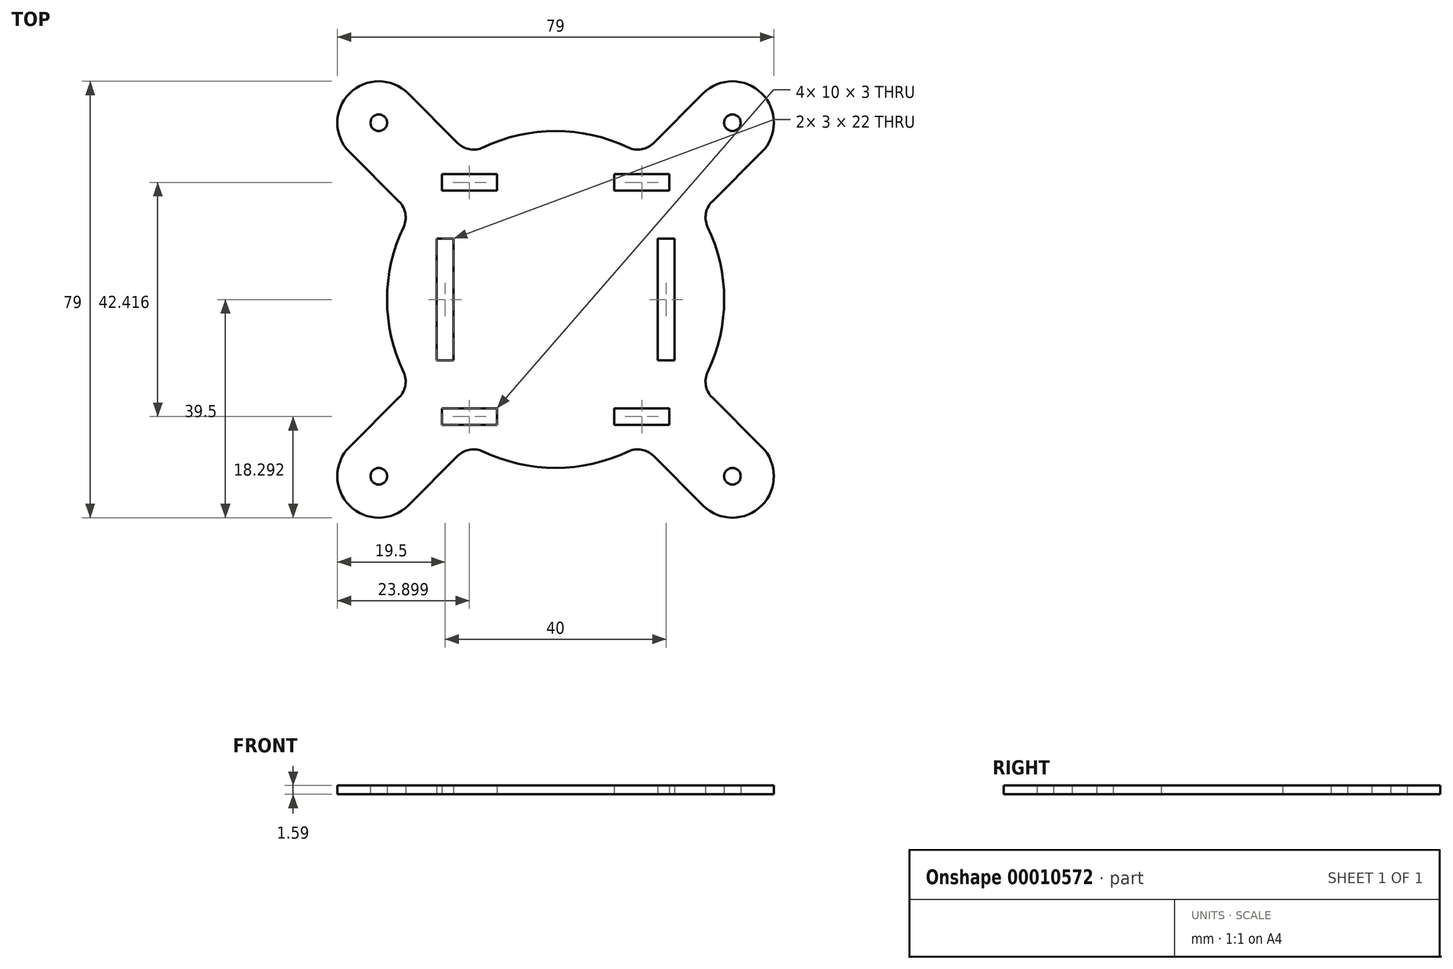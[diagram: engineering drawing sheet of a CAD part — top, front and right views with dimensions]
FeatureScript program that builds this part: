
annotation { "Feature Type Name" : "Feature", "Feature Type Description" : "" }
export const myFeature = defineFeature(function(context is Context, id is Id, definition is map)
    precondition{}
    {
        {
            var Q0;
            Q0=qCreatedBy(makeId("Top.planeOp"),FACE);
            var sketch = newSketch(context, id + "F0", { "sketchPlane" : qUnion([Q0])});
            skCircle(sketch, "E0", {"center": v(-32, -32) * mm, "radius": 1.5 * mm});
            skCircle(sketch, "E1", {"center": v(-32, 32) * mm, "radius": 1.5 * mm});
            skCircle(sketch, "E2", {"center": v(32, 32) * mm, "radius": 1.5 * mm});
            skCircle(sketch, "E3", {"center": v(32, -32) * mm, "radius": 1.5 * mm});
            skLineSegment(sketch, "E4", {"start": v(-32, 32) * mm, "end": v(-32, -32) * mm, "construction": true});
            skLineSegment(sketch, "E5", {"start": v(-32, -32) * mm, "end": v(32, -32) * mm, "construction": true});
            skLineSegment(sketch, "E6", {"start": v(-32, 32) * mm, "end": v(32, 32) * mm, "construction": true});
            skLineSegment(sketch, "E7", {"start": v(32, -32) * mm, "end": v(32, 32) * mm, "construction": true});
            skCircle(sketch, "E8", {"center": v(0, 0) * mm, "radius": 22.5 * mm});
            skCircle(sketch, "E9.0", {"center": v(0, 0) * mm, "radius": 30.5 * mm});
            skCircle(sketch, "E10.0", {"center": v(-32, 32) * mm, "radius": 7.5 * mm});
            skLineSegment(sketch, "E11", {"start": v(-37.3, 26.7) * mm, "end": v(-26.2, 15.6) * mm});
            skLineSegment(sketch, "E12", {"start": v(-26.7, 37.3) * mm, "end": v(-15.6, 26.2) * mm});
            skLineSegment(sketch, "E13", {"start": v(0, 0) * mm, "end": v(-32, 32) * mm, "construction": true});
            skCircle(sketch, "E14", {"center": v(32, 32) * mm, "radius": 7.5 * mm});
            skCircle(sketch, "E15", {"center": v(32, -32) * mm, "radius": 7.5 * mm});
            skCircle(sketch, "E16", {"center": v(-32, -32) * mm, "radius": 7.5 * mm});
            skLineSegment(sketch, "E17", {"start": v(0, 0) * mm, "end": v(32, 32) * mm, "construction": true});
            skLineSegment(sketch, "E18", {"start": v(0, 0) * mm, "end": v(32, -32) * mm, "construction": true});
            skLineSegment(sketch, "E19", {"start": v(0, 0) * mm, "end": v(-32, -32) * mm, "construction": true});
            skLineSegment(sketch, "E20", {"start": v(-37.3, -26.7) * mm, "end": v(-26.2, -15.6) * mm});
            skLineSegment(sketch, "E21", {"start": v(-26.7, -37.3) * mm, "end": v(-15.6, -26.2) * mm});
            skLineSegment(sketch, "E22", {"start": v(26.7, -37.3) * mm, "end": v(15.6, -26.2) * mm});
            skLineSegment(sketch, "E23", {"start": v(37.3, -26.7) * mm, "end": v(26.2, -15.6) * mm});
            skLineSegment(sketch, "E24", {"start": v(37.3, 26.7) * mm, "end": v(26.2, 15.6) * mm});
            skLineSegment(sketch, "E25", {"start": v(26.7, 37.3) * mm, "end": v(15.6, 26.2) * mm});
            skLineSegment(sketch, "E26.rect.bottom", {"start": v(21.5, 11) * mm, "end": v(18.5, 11) * mm});
            skLineSegment(sketch, "E26.rect.top", {"start": v(21.5, -11) * mm, "end": v(18.5, -11) * mm});
            skLineSegment(sketch, "E26.rect.left", {"start": v(21.5, 11) * mm, "end": v(21.5, -11) * mm});
            skLineSegment(sketch, "E26.rect.right", {"start": v(18.5, 11) * mm, "end": v(18.5, -11) * mm});
            skPoint(sketch, "E26.rect.middle", {"position": v(20, 0) * mm});
            skLineSegment(sketch, "E27.rect.bottom", {"start": v(-18.5, 11) * mm, "end": v(-21.5, 11) * mm});
            skLineSegment(sketch, "E27.rect.top", {"start": v(-18.5, -11) * mm, "end": v(-21.5, -11) * mm});
            skLineSegment(sketch, "E27.rect.left", {"start": v(-18.5, 11) * mm, "end": v(-18.5, -11) * mm});
            skLineSegment(sketch, "E27.rect.right", {"start": v(-21.5, 11) * mm, "end": v(-21.5, -11) * mm});
            skPoint(sketch, "E27.rect.middle", {"position": v(-20, 0) * mm});
            skLineSegment(sketch, "E28", {"start": v(-20, 0) * mm, "end": v(20, 0) * mm, "construction": true});
            skLineSegment(sketch, "E29.rect.bottom", {"start": v(20.6, -19.7) * mm, "end": v(10.6, -19.7) * mm});
            skLineSegment(sketch, "E29.rect.top", {"start": v(20.6, -22.7) * mm, "end": v(10.6, -22.7) * mm});
            skLineSegment(sketch, "E29.rect.left", {"start": v(20.6, -19.7) * mm, "end": v(20.6, -22.7) * mm});
            skLineSegment(sketch, "E29.rect.right", {"start": v(10.6, -19.7) * mm, "end": v(10.6, -22.7) * mm});
            skPoint(sketch, "E29.rect.middle", {"position": v(15.6, -21.2) * mm});
            skLineSegment(sketch, "E30.rect.bottom", {"start": v(-10.6, -19.7) * mm, "end": v(-20.6, -19.7) * mm});
            skLineSegment(sketch, "E30.rect.top", {"start": v(-10.6, -22.7) * mm, "end": v(-20.6, -22.7) * mm});
            skLineSegment(sketch, "E30.rect.left", {"start": v(-10.6, -19.7) * mm, "end": v(-10.6, -22.7) * mm});
            skLineSegment(sketch, "E30.rect.right", {"start": v(-20.6, -19.7) * mm, "end": v(-20.6, -22.7) * mm});
            skPoint(sketch, "E30.rect.middle", {"position": v(-15.6, -21.2) * mm});
            skLineSegment(sketch, "E31.rect.bottom", {"start": v(-10.6, 22.7) * mm, "end": v(-20.6, 22.7) * mm});
            skLineSegment(sketch, "E31.rect.top", {"start": v(-10.6, 19.7) * mm, "end": v(-20.6, 19.7) * mm});
            skLineSegment(sketch, "E31.rect.left", {"start": v(-10.6, 22.7) * mm, "end": v(-10.6, 19.7) * mm});
            skLineSegment(sketch, "E31.rect.right", {"start": v(-20.6, 22.7) * mm, "end": v(-20.6, 19.7) * mm});
            skPoint(sketch, "E31.rect.middle", {"position": v(-15.6, 21.2) * mm});
            skLineSegment(sketch, "E32.rect.bottom", {"start": v(20.6, 19.7) * mm, "end": v(10.6, 19.7) * mm});
            skLineSegment(sketch, "E32.rect.top", {"start": v(20.6, 22.7) * mm, "end": v(10.6, 22.7) * mm});
            skLineSegment(sketch, "E32.rect.left", {"start": v(20.6, 19.7) * mm, "end": v(20.6, 22.7) * mm});
            skLineSegment(sketch, "E32.rect.right", {"start": v(10.6, 19.7) * mm, "end": v(10.6, 22.7) * mm});
            skPoint(sketch, "E32.rect.middle", {"position": v(15.6, 21.2) * mm});
            skLineSegment(sketch, "E33", {"start": v(-15.6, -26.2) * mm, "end": v(-15.6, -21.2) * mm, "construction": true});
            skLineSegment(sketch, "E34", {"start": v(-15.6, 21.2) * mm, "end": v(-15.6, 26.2) * mm, "construction": true});
            skSolve(sketch);
        }
        {
            var Q0;
            Q0=makeQuery(id+"F0.imprint","IMPRINT",FACE,{"disambiguationData":[TD([[makeQuery(id+"F0.imprint","IMPRINT",EDGE,{"derivedFrom":sQuery(id+"F0.wireOp",EDGE,"E8")}),-1.0]])]});
            var Q1;
            {var subQ1=sQuery(id+"F0.wireOp",EDGE,"E20");Q1=makeQuery(id+"F0.imprint","IMPRINT",FACE,{"disambiguationData":[TD([[makeQuery(id+"F0.imprint","IMPRINT",EDGE,{"derivedFrom":subQ1}),-1.0]])]});}
            var Q2;
            {var subQ1=sQuery(id+"F0.wireOp",EDGE,"E22");Q2=makeQuery(id+"F0.imprint","IMPRINT",FACE,{"disambiguationData":[TD([[makeQuery(id+"F0.imprint","IMPRINT",EDGE,{"derivedFrom":subQ1}),-1.0]])]});}
            var Q3;
            {var subQ1=sQuery(id+"F0.wireOp",EDGE,"E24");Q3=makeQuery(id+"F0.imprint","IMPRINT",FACE,{"disambiguationData":[TD([[makeQuery(id+"F0.imprint","IMPRINT",EDGE,{"derivedFrom":subQ1}),-1.0]])]});}
            var Q4;
            Q4=makeQuery(id+"F0.imprint","IMPRINT",FACE,{"disambiguationData":[TD([[makeQuery(id+"F0.imprint","IMPRINT",EDGE,{"derivedFrom":sQuery(id+"F0.wireOp",EDGE,"E0")}),-1.0]])]});
            var Q5;
            Q5=makeQuery(id+"F0.imprint","IMPRINT",FACE,{"disambiguationData":[TD([[makeQuery(id+"F0.imprint","IMPRINT",EDGE,{"derivedFrom":sQuery(id+"F0.wireOp",EDGE,"E3")}),-1.0]])]});
            var Q6;
            Q6=makeQuery(id+"F0.imprint","IMPRINT",FACE,{"disambiguationData":[TD([[makeQuery(id+"F0.imprint","IMPRINT",EDGE,{"derivedFrom":sQuery(id+"F0.wireOp",EDGE,"E2")}),-1.0]])]});
            var Q7;
            Q7=makeQuery(id+"F0.imprint","IMPRINT",FACE,{"disambiguationData":[TD([[makeQuery(id+"F0.imprint","IMPRINT",EDGE,{"derivedFrom":sQuery(id+"F0.wireOp",EDGE,"E1")}),-1.0]])]});
            var Q8;
            {var subQ1=sQuery(id+"F0.wireOp",EDGE,"E11");Q8=makeQuery(id+"F0.imprint","IMPRINT",FACE,{"disambiguationData":[TD([[makeQuery(id+"F0.imprint","IMPRINT",EDGE,{"derivedFrom":subQ1}),1.0]])]});}
            var Q9;
            Q9=makeQuery(id+"F0.imprint","IMPRINT",FACE,{"disambiguationData":[TD([[makeQuery(id+"F0.imprint","IMPRINT",EDGE,{"derivedFrom":sQuery(id+"F0.wireOp",EDGE,"E8")}),1.0]])]});
            var Q10;
            {var subQ4=sQuery(id+"F0.wireOp",EDGE,"E26.rect.right");Q10=makeQuery(id+"F0.imprint","IMPRINT",FACE,{"disambiguationData":[TD([[makeQuery(id+"F0.imprint","IMPRINT",EDGE,{"derivedFrom":subQ4}),-1.0]])]});}
            var Q11;
            {var subQ1=sQuery(id+"F0.wireOp",EDGE,"E8");var subQ11=sQuery(id+"F0.wireOp",EDGE,"E30.rect.left");var subQ13=makeQuery(id+"F0.imprint","INTERSECT",VERTEX,{"derivedFrom":[subQ1,subQ11]});Q11=makeQuery(id+"F0.imprint","IMPRINT",FACE,{"disambiguationData":[TD([[makeQuery(id+"F0.imprint","IMPRINT",EDGE,{"disambiguationData":[TD([[subQ13,-1.0]])],"derivedFrom":subQ1}),-1.0]])]});}
            var Q12;
            {var subQ0=sQuery(id+"F0.wireOp",EDGE,"E32.rect.right");var subQ1=sQuery(id+"F0.wireOp",EDGE,"E8");var subQ2=makeQuery(id+"F0.imprint","INTERSECT",VERTEX,{"derivedFrom":[subQ1,subQ0]});Q12=makeQuery(id+"F0.imprint","IMPRINT",FACE,{"disambiguationData":[TD([[makeQuery(id+"F0.imprint","IMPRINT",EDGE,{"disambiguationData":[TD([[subQ2,-1.0]])],"derivedFrom":subQ1}),-1.0]])]});}
            var Q13;
            {var subQ0=sQuery(id+"F0.wireOp",EDGE,"E27.rect.right");var subQ1=sQuery(id+"F0.wireOp",EDGE,"E8");var subQ3=makeQuery(id+"F0.imprint","INTERSECT",VERTEX,{"disambiguationData":[OD(0.0)],"derivedFrom":[subQ1,subQ0]});Q13=makeQuery(id+"F0.imprint","IMPRINT",FACE,{"disambiguationData":[TD([[makeQuery(id+"F0.imprint","IMPRINT",EDGE,{"disambiguationData":[TD([[subQ3,-1.0]])],"derivedFrom":subQ1}),1.0]])]});}
            var Q14;
            {var subQ0=sQuery(id+"F0.wireOp",EDGE,"E26.rect.left");var subQ1=sQuery(id+"F0.wireOp",EDGE,"E8");var subQ3=makeQuery(id+"F0.imprint","INTERSECT",VERTEX,{"disambiguationData":[OD(0.0)],"derivedFrom":[subQ1,subQ0]});Q14=makeQuery(id+"F0.imprint","IMPRINT",FACE,{"disambiguationData":[TD([[makeQuery(id+"F0.imprint","IMPRINT",EDGE,{"disambiguationData":[TD([[subQ3,1.0]])],"derivedFrom":subQ1}),1.0]])]});}
            extrude(context, id + "F1", {"entities" : qUnion([Q0, Q1, Q2, Q3, Q4, Q5, Q6, Q7, Q8, Q9, Q10, Q11, Q12, Q13, Q14]), "depth" : 1.59 * mm});
        }
        {
            var Q0;
            Q0=makeQuery(id+"F1.opExtrude","SWEPT_EDGE",EDGE,{"disambiguationData":[OSD([sQuery(id+"F0.wireOp",EDGE,"E9.0"),sQuery(id+"F0.wireOp",EDGE,"E21")])]});
            var Q1;
            Q1=makeQuery(id+"F1.opExtrude","SWEPT_EDGE",EDGE,{"disambiguationData":[OSD([sQuery(id+"F0.wireOp",EDGE,"E9.0"),sQuery(id+"F0.wireOp",EDGE,"E22")])]});
            var Q2;
            Q2=makeQuery(id+"F1.opExtrude","SWEPT_EDGE",EDGE,{"disambiguationData":[OSD([sQuery(id+"F0.wireOp",EDGE,"E9.0"),sQuery(id+"F0.wireOp",EDGE,"E23")])]});
            var Q3;
            Q3=makeQuery(id+"F1.opExtrude","SWEPT_EDGE",EDGE,{"disambiguationData":[OSD([sQuery(id+"F0.wireOp",EDGE,"E9.0"),sQuery(id+"F0.wireOp",EDGE,"E24")])]});
            var Q4;
            Q4=makeQuery(id+"F1.opExtrude","SWEPT_EDGE",EDGE,{"disambiguationData":[OSD([sQuery(id+"F0.wireOp",EDGE,"E9.0"),sQuery(id+"F0.wireOp",EDGE,"E25")])]});
            var Q5;
            Q5=makeQuery(id+"F1.opExtrude","SWEPT_EDGE",EDGE,{"disambiguationData":[OSD([sQuery(id+"F0.wireOp",EDGE,"E9.0"),sQuery(id+"F0.wireOp",EDGE,"E12")])]});
            var Q6;
            Q6=makeQuery(id+"F1.opExtrude","SWEPT_EDGE",EDGE,{"disambiguationData":[OSD([sQuery(id+"F0.wireOp",EDGE,"E9.0"),sQuery(id+"F0.wireOp",EDGE,"E11")])]});
            var Q7;
            Q7=makeQuery(id+"F1.opExtrude","SWEPT_EDGE",EDGE,{"disambiguationData":[OSD([sQuery(id+"F0.wireOp",EDGE,"E9.0"),sQuery(id+"F0.wireOp",EDGE,"E20")])]});
            fillet(context, id + "F2", {"entities" : qUnion([Q0, Q1, Q2, Q3, Q4, Q5, Q6, Q7]), "radius" : 4 * mm, "tangentPropagation" : true, "allowEdgeOverflow" : false});
        }
    });
